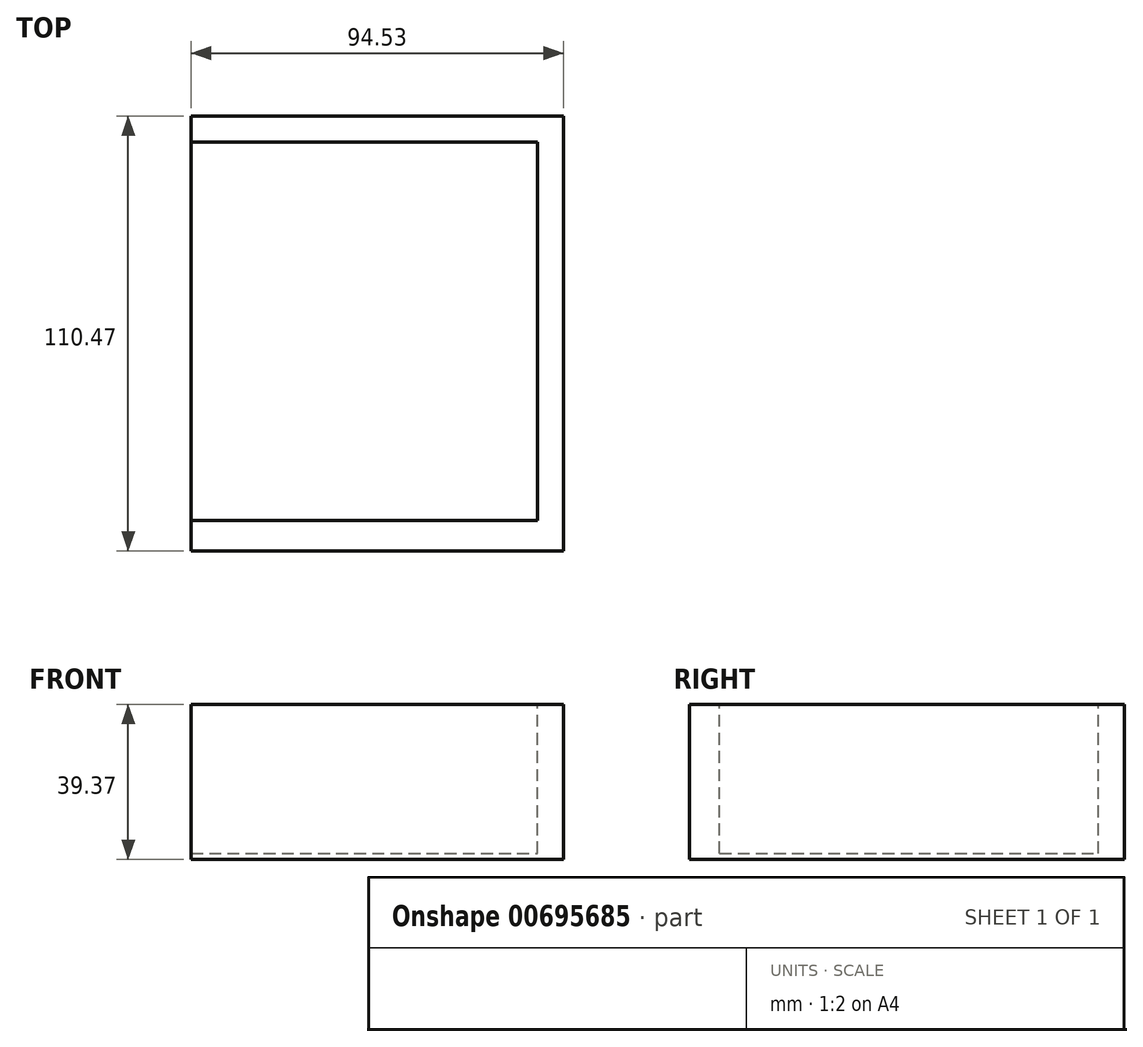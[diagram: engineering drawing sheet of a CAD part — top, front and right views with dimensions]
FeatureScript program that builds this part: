
annotation { "Feature Type Name" : "Feature", "Feature Type Description" : "" }
export const myFeature = defineFeature(function(context is Context, id is Id, definition is map)
    precondition{}
    {
        {
            var Q0;
            Q0=qCreatedBy(makeId("Top.planeOp"),FACE);
            var sketch = newSketch(context, id + "F0", { "sketchPlane" : qUnion([Q0])});
            skLineSegment(sketch, "E0.bottom", {"start": v(-52.93, -52.22) * mm, "end": v(49.4, -52.22) * mm});
            skLineSegment(sketch, "E0.top", {"start": v(-52.93, 58.25) * mm, "end": v(49.4, 58.25) * mm});
            skLineSegment(sketch, "E0.left", {"start": v(-52.93, -52.22) * mm, "end": v(-52.93, 58.25) * mm});
            skLineSegment(sketch, "E0.right", {"start": v(49.4, -52.22) * mm, "end": v(49.4, 58.25) * mm});
            skSolve(sketch);
        }
        {
            var Q0;
            Q0=makeQuery(id+"F0.imprint","IMPRINT",FACE,{"disambiguationData":[TD([[makeQuery(id+"F0.imprint","IMPRINT",EDGE,{"derivedFrom":sQuery(id+"F0.wireOp",EDGE,"E0.bottom")}),1.0]])]});
            extrude(context, id + "F1", {"entities" : qUnion([Q0]), "oppositeDirection" : true, "depth" : 39.37 * mm, "offsetDistance" : 25.4 * mm});
        }
        {
            var Q0;
            Q0=makeQuery(id+"F1.opExtrude","CAP_FACE",FACE,{"disambiguationData":[OSD([sQuery(id+"F0.wireOp",EDGE,"E0.bottom"),sQuery(id+"F0.wireOp",EDGE,"E0.top"),sQuery(id+"F0.wireOp",EDGE,"E0.left"),sQuery(id+"F0.wireOp",EDGE,"E0.right")])],"isStart":true});
            var sketch = newSketch(context, id + "F2", { "sketchPlane" : qUnion([Q0])});
            skLineSegment(sketch, "E1.bottom", {"start": v(-45.16, -44.52) * mm, "end": v(42.87, -44.52) * mm});
            skLineSegment(sketch, "E1.top", {"start": v(-45.16, 51.67) * mm, "end": v(42.87, 51.67) * mm});
            skLineSegment(sketch, "E1.left", {"start": v(-45.16, -44.52) * mm, "end": v(-45.16, 51.67) * mm});
            skLineSegment(sketch, "E1.right", {"start": v(42.87, -44.52) * mm, "end": v(42.87, 51.67) * mm});
            skSolve(sketch);
        }
        {
            var Q0;
            Q0 = qSketchRegion(id + "F2", true);
            extrude(context, id + "F3", {"entities" : qUnion([Q0]), "operationType" : NewBodyOperationType.REMOVE, "oppositeDirection" : true, "depth" : 37.85 * mm, "offsetDistance" : 25.4 * mm});
        }
        {
            var Q0;
            Q0=qCreatedBy(makeId("Top.planeOp"),FACE);
            var sketch = newSketch(context, id + "F4", { "sketchPlane" : qUnion([Q0])});
            skLineSegment(sketch, "E2.bottom", {"start": v(-45.13, -52.53) * mm, "end": v(-73.96, -52.53) * mm});
            skLineSegment(sketch, "E2.top", {"start": v(-45.13, 88.24) * mm, "end": v(-73.96, 88.24) * mm});
            skLineSegment(sketch, "E2.left", {"start": v(-45.13, -52.53) * mm, "end": v(-45.13, 88.24) * mm});
            skLineSegment(sketch, "E2.right", {"start": v(-73.96, -52.53) * mm, "end": v(-73.96, 88.24) * mm});
            skSolve(sketch);
        }
        {
            var Q0;
            Q0 = qSketchRegion(id + "F4", true);
            extrude(context, id + "F5", {"entities" : qUnion([Q0]), "operationType" : NewBodyOperationType.REMOVE, "oppositeDirection" : true, "depth" : 58.17 * mm, "offsetDistance" : 25.4 * mm});
        }
    });
